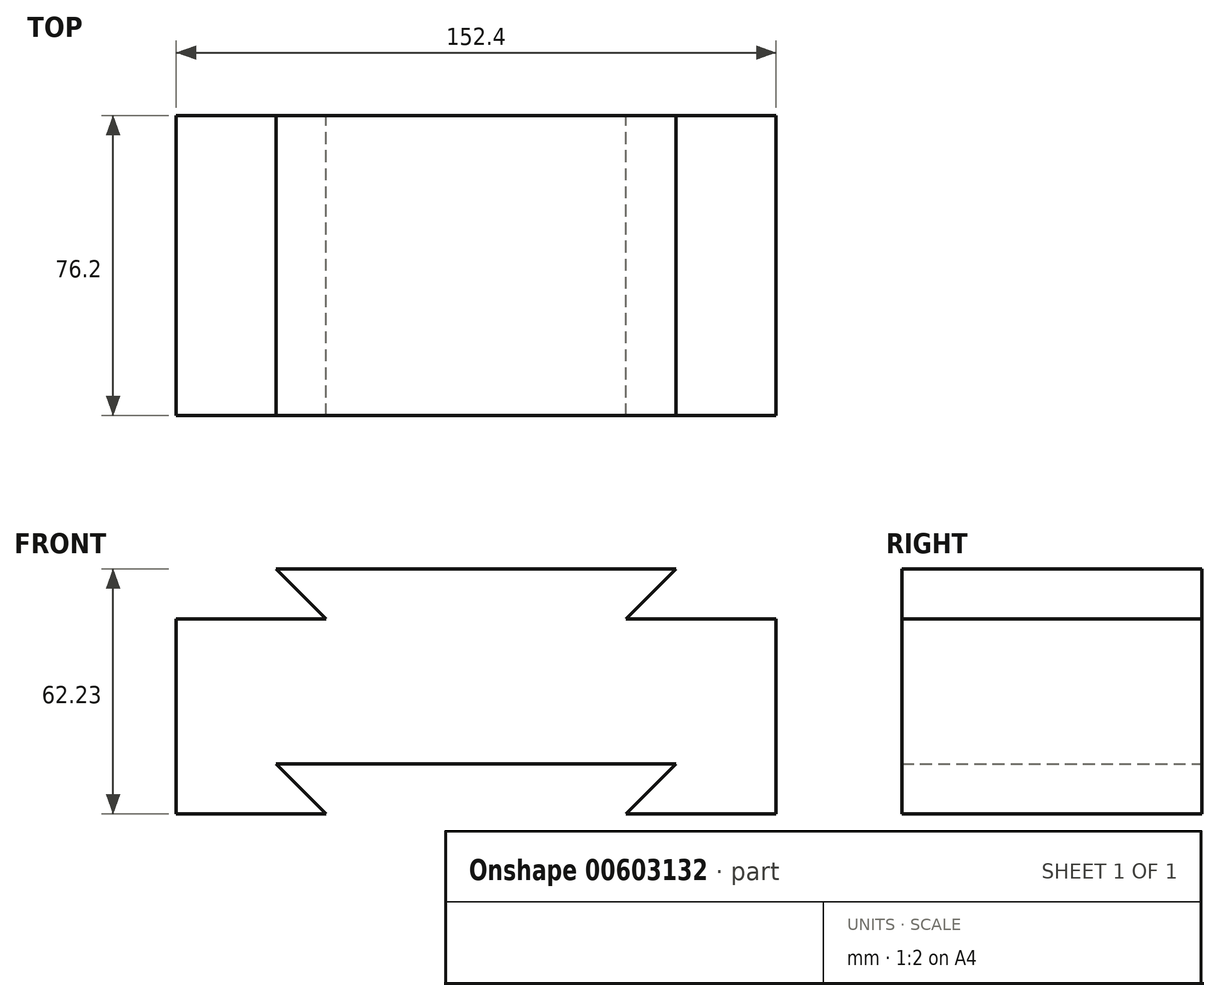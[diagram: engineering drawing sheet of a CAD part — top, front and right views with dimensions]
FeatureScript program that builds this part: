
annotation { "Feature Type Name" : "Feature", "Feature Type Description" : "" }
export const myFeature = defineFeature(function(context is Context, id is Id, definition is map)
    precondition{}
    {
        {
            var Q0;
            Q0=qCreatedBy(makeId("Front.planeOp"),FACE);
            var sketch = newSketch(context, id + "F0", { "sketchPlane" : qUnion([Q0])});
            skLineSegment(sketch, "E0", {"start": v(-59.12, 62.08) * mm, "end": v(42.48, 62.08) * mm});
            skLineSegment(sketch, "E1", {"start": v(42.48, 49.38) * mm, "end": v(67.88, 49.38) * mm});
            skLineSegment(sketch, "E2", {"start": v(67.88, 49.38) * mm, "end": v(67.88, -0.15) * mm});
            skLineSegment(sketch, "E3", {"start": v(67.88, -0.15) * mm, "end": v(29.78, -0.15) * mm});
            skLineSegment(sketch, "E4", {"start": v(29.78, 12.55) * mm, "end": v(-46.42, 12.55) * mm});
            skLineSegment(sketch, "E5", {"start": v(-46.42, -0.15) * mm, "end": v(-84.52, -0.15) * mm});
            skLineSegment(sketch, "E6", {"start": v(-84.52, -0.15) * mm, "end": v(-84.52, 49.38) * mm});
            skLineSegment(sketch, "E7", {"start": v(-84.52, 49.38) * mm, "end": v(-59.12, 49.38) * mm});
            skLineSegment(sketch, "E8", {"start": v(-59.12, 12.55) * mm, "end": v(-46.42, 12.55) * mm});
            skLineSegment(sketch, "E9", {"start": v(42.48, 12.55) * mm, "end": v(29.78, 12.55) * mm});
            skLineSegment(sketch, "E10", {"start": v(-59.12, 12.55) * mm, "end": v(-46.42, -0.15) * mm});
            skLineSegment(sketch, "E11", {"start": v(42.48, 12.55) * mm, "end": v(29.78, -0.15) * mm});
            skLineSegment(sketch, "E12", {"start": v(29.78, 49.38) * mm, "end": v(42.48, 49.38) * mm});
            skLineSegment(sketch, "E13", {"start": v(-59.12, 49.38) * mm, "end": v(-46.42, 49.38) * mm});
            skLineSegment(sketch, "E14", {"start": v(42.48, 62.08) * mm, "end": v(29.78, 49.38) * mm});
            skLineSegment(sketch, "E15", {"start": v(-59.12, 62.08) * mm, "end": v(-46.42, 49.38) * mm});
            skSolve(sketch);
        }
        {
            var Q0;
            Q0=makeQuery(id+"F0.imprint","IMPRINT",FACE,{"disambiguationData":[TD([[makeQuery(id+"F0.imprint","IMPRINT",EDGE,{"derivedFrom":sQuery(id+"F0.wireOp",EDGE,"E0")}),-1.0]])]});
            extrude(context, id + "F1", {"entities" : qUnion([Q0]), "depth" : 76.2 * mm, "offsetDistance" : 25.4 * mm});
        }
    });
